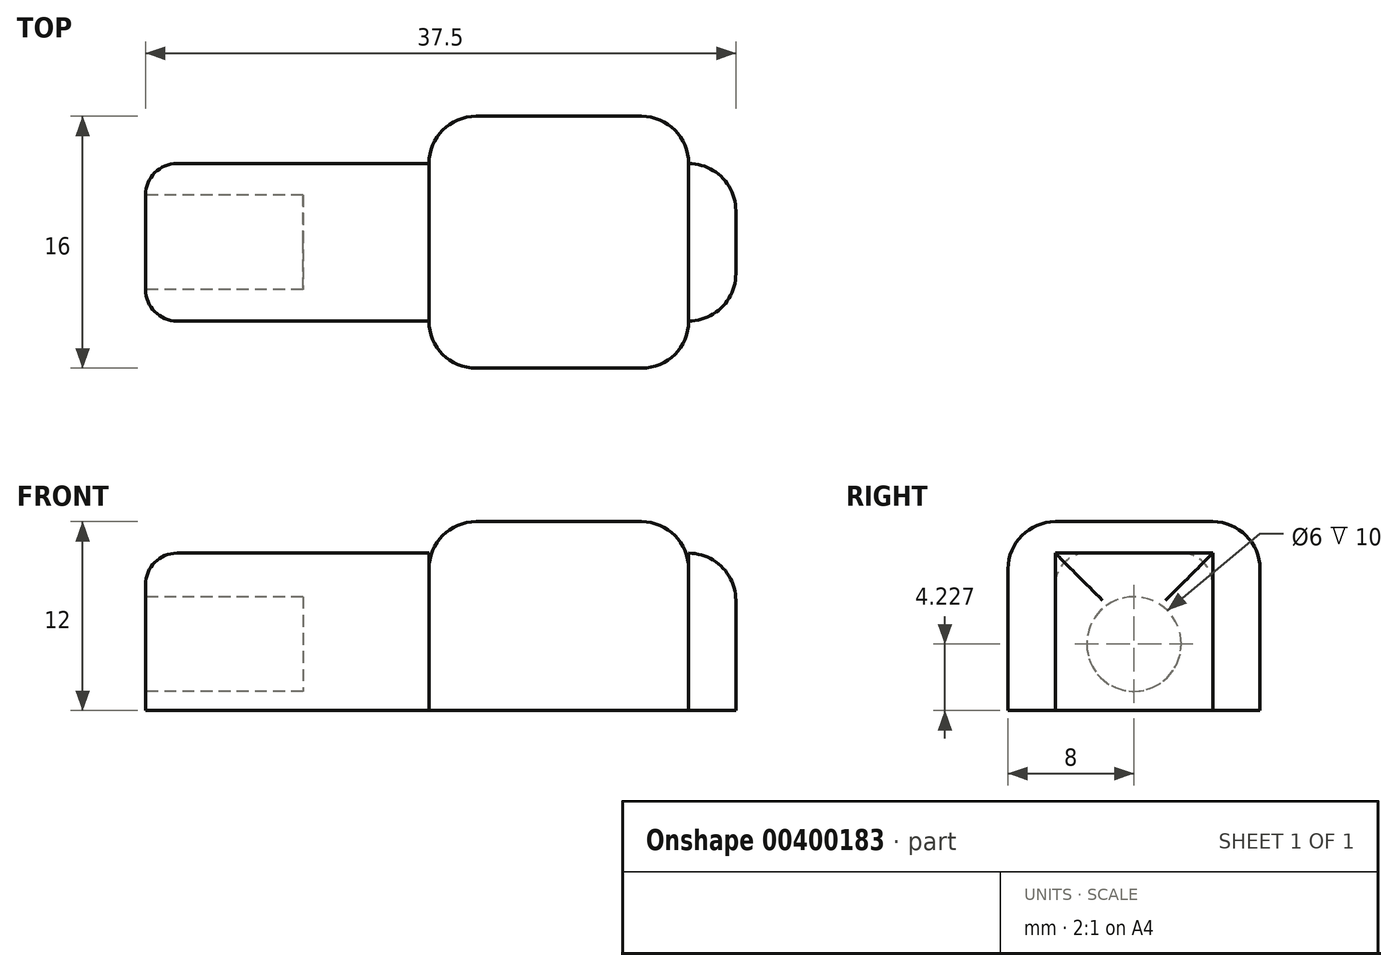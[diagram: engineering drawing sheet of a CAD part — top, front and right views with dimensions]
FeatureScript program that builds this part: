
annotation { "Feature Type Name" : "Feature", "Feature Type Description" : "" }
export const myFeature = defineFeature(function(context is Context, id is Id, definition is map)
    precondition{}
    {
        {
            var Q0;
            Q0=qCreatedBy(makeId("Top.planeOp"),FACE);
            var sketch = newSketch(context, id + "F0", { "sketchPlane" : qUnion([Q0])});
            skLineSegment(sketch, "E0.bottom", {"start": v(-28, 0) * mm, "end": v(-10, 0) * mm});
            skLineSegment(sketch, "E0.top", {"start": v(-28, 10) * mm, "end": v(-10, 10) * mm});
            skLineSegment(sketch, "E0.left", {"start": v(-28, 0) * mm, "end": v(-28, 10) * mm});
            skLineSegment(sketch, "E0.right", {"start": v(-10, 0) * mm, "end": v(-10, 10) * mm});
            skLineSegment(sketch, "E1.bottom", {"start": v(-10, -3) * mm, "end": v(6.5, -3) * mm});
            skLineSegment(sketch, "E1.top", {"start": v(-10, 13) * mm, "end": v(6.5, 13) * mm});
            skLineSegment(sketch, "E1.left", {"start": v(-10, -3) * mm, "end": v(-10, 13) * mm});
            skLineSegment(sketch, "E1.right", {"start": v(6.5, -3) * mm, "end": v(6.5, 13) * mm});
            skLineSegment(sketch, "E2.bottom", {"start": v(6.5, 0) * mm, "end": v(9.5, 0) * mm});
            skLineSegment(sketch, "E2.top", {"start": v(6.5, 10) * mm, "end": v(9.5, 10) * mm});
            skLineSegment(sketch, "E2.left", {"start": v(6.5, 0) * mm, "end": v(6.5, 10) * mm});
            skLineSegment(sketch, "E2.right", {"start": v(9.5, 0) * mm, "end": v(9.5, 10) * mm});
            skSolve(sketch);
        }
        {
            var Q0;
            {var subQ0=sQuery(id+"F0.wireOp",EDGE,"E0.bottom");Q0=makeQuery(id+"F0.imprint","IMPRINT",FACE,{"disambiguationData":[TD([[makeQuery(id+"F0.imprint","IMPRINT",EDGE,{"derivedFrom":subQ0}),1.0]])]});}
            var Q1;
            Q1=makeQuery(id+"F0.imprint","IMPRINT",FACE,{"disambiguationData":[TD([[makeQuery(id+"F0.imprint","IMPRINT",EDGE,{"derivedFrom":sQuery(id+"F0.wireOp",EDGE,"E2.bottom")}),1.0]])]});
            extrude(context, id + "F1", {"entities" : qUnion([Q0, Q1]), "depth" : 10 * mm});
        }
        {
            var Q0;
            {var subQ3=sQuery(id+"F0.wireOp",EDGE,"E1.bottom");Q0=makeQuery(id+"F0.imprint","IMPRINT",FACE,{"disambiguationData":[TD([[makeQuery(id+"F0.imprint","IMPRINT",EDGE,{"derivedFrom":subQ3}),1.0]])]});}
            extrude(context, id + "F2", {"entities" : qUnion([Q0]), "depth" : 12 * mm});
        }
        {
            var Q0;
            Q0=makeQuery(id+"F1.opExtrude","CAP_EDGE",EDGE,{"disambiguationData":[OSD([sQuery(id+"F0.wireOp",EDGE,"E0.bottom")])],"isStart":false});
            var Q1;
            Q1=makeQuery(id+"F1.opExtrude","SWEPT_EDGE",EDGE,{"disambiguationData":[OSD([sQuery(id+"F0.wireOp",EDGE,"E0.bottom"),sQuery(id+"F0.wireOp",EDGE,"E0.left")])]});
            var Q2;
            Q2=makeQuery(id+"F1.opExtrude","CAP_EDGE",EDGE,{"disambiguationData":[OSD([sQuery(id+"F0.wireOp",EDGE,"E0.left")])],"isStart":false});
            var Q3;
            Q3=makeQuery(id+"F1.opExtrude","SWEPT_EDGE",EDGE,{"disambiguationData":[OSD([sQuery(id+"F0.wireOp",EDGE,"E0.top"),sQuery(id+"F0.wireOp",EDGE,"E0.left")])]});
            var Q4;
            Q4=makeQuery(id+"F1.opExtrude","CAP_EDGE",EDGE,{"disambiguationData":[OSD([sQuery(id+"F0.wireOp",EDGE,"E0.top")])],"isStart":false});
            fillet(context, id + "F3", {"entities" : qUnion([Q0, Q1, Q2, Q3, Q4]), "radius" : 2 * mm, "tangentPropagation" : true, "allowEdgeOverflow" : false});
        }
        {
            var Q0;
            Q0=makeQuery(id+"F2.opExtrude","CAP_FACE",FACE,{"disambiguationData":[OSD([sQuery(id+"F0.wireOp",EDGE,"E1.bottom"),sQuery(id+"F0.wireOp",EDGE,"E1.top"),sQuery(id+"F0.wireOp",EDGE,"E1.left"),sQuery(id+"F0.wireOp",EDGE,"E1.right"),sQuery(id+"F0.wireOp",EDGE,"E2.left")])],"isStart":false});
            var Q1;
            Q1=makeQuery(id+"F2.opExtrude","SWEPT_EDGE",EDGE,{"disambiguationData":[OSD([sQuery(id+"F0.wireOp",EDGE,"E1.bottom"),sQuery(id+"F0.wireOp",EDGE,"E1.right")])]});
            var Q2;
            Q2=makeQuery(id+"F2.opExtrude","SWEPT_EDGE",EDGE,{"disambiguationData":[OSD([sQuery(id+"F0.wireOp",EDGE,"E1.bottom"),sQuery(id+"F0.wireOp",EDGE,"E1.left")])]});
            var Q3;
            Q3=makeQuery(id+"F2.opExtrude","SWEPT_EDGE",EDGE,{"disambiguationData":[OSD([sQuery(id+"F0.wireOp",EDGE,"E1.top"),sQuery(id+"F0.wireOp",EDGE,"E1.left")])]});
            var Q4;
            Q4=makeQuery(id+"F2.opExtrude","SWEPT_EDGE",EDGE,{"disambiguationData":[OSD([sQuery(id+"F0.wireOp",EDGE,"E1.top"),sQuery(id+"F0.wireOp",EDGE,"E1.right")])]});
            fillet(context, id + "F4", {"entities" : qUnion([Q0, Q1, Q2, Q3, Q4]), "radius" : 3 * mm, "tangentPropagation" : true, "allowEdgeOverflow" : false});
        }
        {
            var Q0;
            Q0=makeQuery(id+"F1.opExtrude","CAP_EDGE",EDGE,{"disambiguationData":[OSD([sQuery(id+"F0.wireOp",EDGE,"E2.right")])],"isStart":false});
            var Q1;
            Q1=makeQuery(id+"F1.opExtrude","SWEPT_EDGE",EDGE,{"disambiguationData":[OSD([sQuery(id+"F0.wireOp",EDGE,"E2.bottom"),sQuery(id+"F0.wireOp",EDGE,"E2.right")])]});
            var Q2;
            Q2=makeQuery(id+"F1.opExtrude","SWEPT_EDGE",EDGE,{"disambiguationData":[OSD([sQuery(id+"F0.wireOp",EDGE,"E2.top"),sQuery(id+"F0.wireOp",EDGE,"E2.right")])]});
            fillet(context, id + "F5", {"entities" : qUnion([Q0, Q1, Q2]), "radius" : 3 * mm, "tangentPropagation" : true, "allowEdgeOverflow" : false});
        }
        {
            var Q0;
            Q0=makeQuery(id+"F1.opExtrude","SWEPT_FACE",FACE,{"disambiguationData":[OSD([sQuery(id+"F0.wireOp",EDGE,"E0.left")])]});
            var sketch = newSketch(context, id + "F6", { "sketchPlane" : qUnion([Q0])});
            skLineSegment(sketch, "E3", {"start": v(-5, 0) * mm, "end": v(-5, 8.45) * mm, "construction": true});
            skPoint(sketch, "E3.endSnap0", {"position": v(-5, 8) * mm});
            skCircle(sketch, "E4", {"center": v(-5, 4.23) * mm, "radius": 3 * mm});
            skSolve(sketch);
        }
        {
            var Q0;
            {var subQ0=sQuery(id+"F6.wireOp",EDGE,"E4");var subQ1=sQuery(id+"F0.wireOp",EDGE,"E0.left");var subQ2=makeQuery(id+"F1.opExtrude","SWEPT_FACE",FACE,{"disambiguationData":[OSD([subQ1])]});var subQ3=makeQuery(id+"F6.imprint","INTERSECT",VERTEX,{"derivedFrom":[makeQuery(id+"F3.opFillet","BLEND_EDGE",EDGE,{"blendedFrom":[makeQuery(id+"F1.opExtrude","SWEPT_EDGE",EDGE,{"disambiguationData":[OSD([sQuery(id+"F0.wireOp",EDGE,"E0.bottom"),subQ1])]}),subQ2],"blendedInto":[subQ2]}),subQ0]});Q0=makeQuery(id+"F6.imprint","IMPRINT",FACE,{"disambiguationData":[TD([[makeQuery(id+"F6.imprint","IMPRINT",EDGE,{"disambiguationData":[TD([[subQ3,-1.0]])],"derivedFrom":subQ0}),1.0]])]});}
            extrude(context, id + "F7", {"entities" : qUnion([Q0]), "operationType" : NewBodyOperationType.REMOVE, "oppositeDirection" : true, "depth" : 10 * mm});
        }
    });
